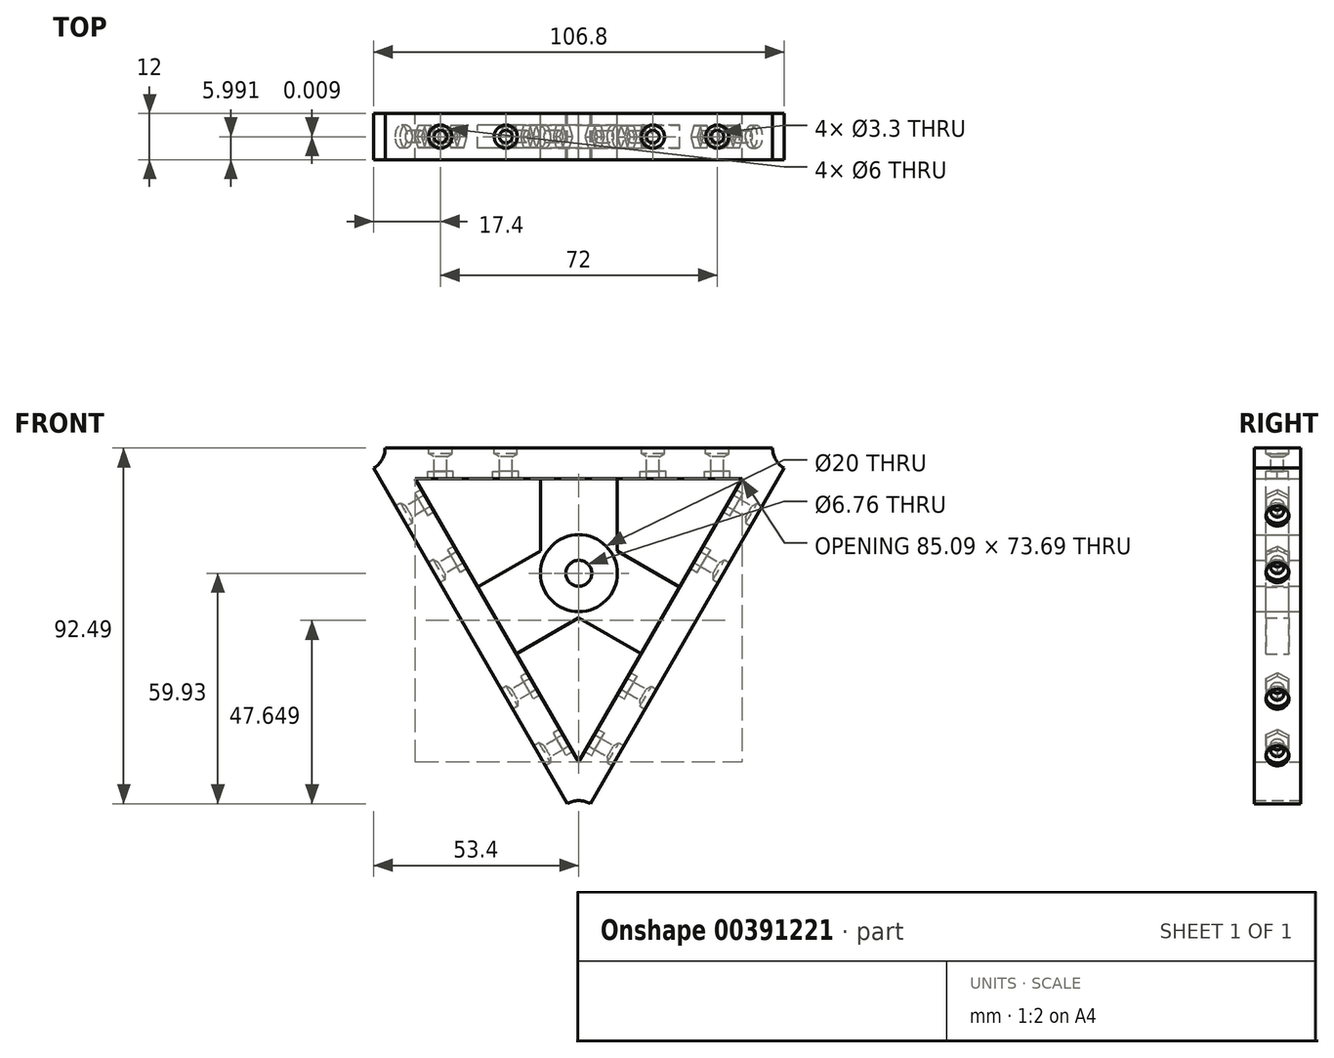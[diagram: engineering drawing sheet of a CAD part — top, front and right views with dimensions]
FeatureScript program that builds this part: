
annotation { "Feature Type Name" : "Feature", "Feature Type Description" : "" }
export const myFeature = defineFeature(function(context is Context, id is Id, definition is map)
    precondition{}
    {
        {
            var Q0;
            Q0=qCreatedBy(makeId("Front.planeOp"),FACE);
            var sketch = newSketch(context, id + "F0", { "sketchPlane" : qUnion([Q0])});
            skCircle(sketch, "E0.cCircle", {"center": v(0, 0) * mm, "radius": 32.56 * mm, "construction": true});
            skLineSegment(sketch, "E0.0", {"start": v(56.4, 32.56) * mm, "end": v(0, -65.13) * mm});
            skLineSegment(sketch, "E0.1", {"start": v(0, -65.13) * mm, "end": v(-56.4, 32.56) * mm});
            skLineSegment(sketch, "E0.2", {"start": v(-56.4, 32.56) * mm, "end": v(56.4, 32.56) * mm});
            skPoint(sketch, "E0.0.midPoint", {"position": v(28.2, -16.28) * mm});
            skCircle(sketch, "E1.cCircle", {"center": v(0, 0) * mm, "radius": 24.56 * mm, "construction": true});
            skLineSegment(sketch, "E1.0", {"start": v(42.54, 24.56) * mm, "end": v(0, -49.13) * mm});
            skLineSegment(sketch, "E1.1", {"start": v(0, -49.13) * mm, "end": v(-42.54, 24.56) * mm});
            skLineSegment(sketch, "E1.2", {"start": v(-42.54, 24.56) * mm, "end": v(42.54, 24.56) * mm});
            skPoint(sketch, "E1.0.midPoint", {"position": v(21.27, -12.28) * mm});
            skCircle(sketch, "E2", {"center": v(56.4, 32.56) * mm, "radius": 6 * mm});
            skCircle(sketch, "E3", {"center": v(-56.4, 32.56) * mm, "radius": 6 * mm});
            skCircle(sketch, "E4", {"center": v(0, -65.13) * mm, "radius": 6 * mm});
            skPoint(sketch, "E5", {"position": v(40.38, 48.53) * mm});
            skPoint(sketch, "E6", {"position": v(46.2, 14.9) * mm});
            skPoint(sketch, "E7", {"position": v(37.7, 0.17) * mm});
            skPoint(sketch, "E8", {"position": v(10.2, -47.46) * mm});
            skPoint(sketch, "E9", {"position": v(18.7, -32.74) * mm});
            skPoint(sketch, "E10", {"position": v(25.9, -20.26) * mm});
            skPoint(sketch, "E11", {"position": v(30.5, -12.3) * mm});
            skCircle(sketch, "E12", {"center": v(0, 0) * mm, "radius": 10 * mm});
            skLineSegment(sketch, "E13", {"start": v(-10, 0) * mm, "end": v(-10, 24.56) * mm});
            skLineSegment(sketch, "E14", {"start": v(10, 0) * mm, "end": v(10, 24.56) * mm});
            skLineSegment(sketch, "E15", {"start": v(5, 8.66) * mm, "end": v(26.27, -3.62) * mm});
            skLineSegment(sketch, "E16", {"start": v(-5, -8.66) * mm, "end": v(16.27, -20.94) * mm});
            skLineSegment(sketch, "E17", {"start": v(-5, 8.66) * mm, "end": v(-26.27, -3.62) * mm});
            skLineSegment(sketch, "E18", {"start": v(5, -8.66) * mm, "end": v(-16.27, -20.94) * mm});
            skSolve(sketch);
        }
        {
            var Q0;
            {var subQ9=sQuery(id+"F0.wireOp",EDGE,"E2");var subQ10=sQuery(id+"F0.wireOp",EDGE,"E0.0");var subQ11=makeQuery(id+"F0.imprint","INTERSECT",VERTEX,{"derivedFrom":[subQ10,subQ9]});Q0=makeQuery(id+"F0.imprint","IMPRINT",FACE,{"disambiguationData":[TD([[makeQuery(id+"F0.imprint","IMPRINT",EDGE,{"disambiguationData":[TD([[subQ11,-1.0]])],"derivedFrom":subQ10}),-1.0]])]});}
            var Q1;
            {var subQ0=sQuery(id+"F0.wireOp",EDGE,"E12");var subQ5=makeQuery(id+"F0.imprint","INTERSECT",VERTEX,{"derivedFrom":[subQ0,sQuery(id+"F0.wireOp",EDGE,"E14")]});Q1=makeQuery(id+"F0.imprint","IMPRINT",FACE,{"disambiguationData":[TD([[makeQuery(id+"F0.imprint","IMPRINT",EDGE,{"disambiguationData":[TD([[subQ5,-1.0]])],"derivedFrom":subQ0}),1.0]])]});}
            extrude(context, id + "F1", {"entities" : qUnion([Q0, Q1]), "depth" : 12 * mm});
        }
        {
            var Q0;
            {var subQ1=sQuery(id+"F0.wireOp",EDGE,"E1.2");var subQ9=sQuery(id+"F0.wireOp",EDGE,"E13");var subQ10=makeQuery(id+"F0.imprint","INTERSECT",VERTEX,{"derivedFrom":[subQ1,subQ9]});Q0=makeQuery(id+"F0.imprint","IMPRINT",FACE,{"disambiguationData":[TD([[makeQuery(id+"F0.imprint","IMPRINT",EDGE,{"disambiguationData":[TD([[subQ10,-1.0]])],"derivedFrom":subQ1}),-1.0]])]});}
            var Q1;
            {var subQ3=sQuery(id+"F0.wireOp",EDGE,"E15");var subQ5=sQuery(id+"F0.wireOp",EDGE,"E1.0");var subQ6=makeQuery(id+"F0.imprint","INTERSECT",VERTEX,{"derivedFrom":[subQ5,subQ3]});Q1=makeQuery(id+"F0.imprint","IMPRINT",FACE,{"disambiguationData":[TD([[makeQuery(id+"F0.imprint","IMPRINT",EDGE,{"disambiguationData":[TD([[subQ6,-1.0]])],"derivedFrom":subQ5}),-1.0]])]});}
            var Q2;
            {var subQ7=sQuery(id+"F0.wireOp",EDGE,"E17");var subQ9=sQuery(id+"F0.wireOp",EDGE,"E1.1");var subQ11=makeQuery(id+"F0.imprint","INTERSECT",VERTEX,{"derivedFrom":[subQ9,subQ7]});Q2=makeQuery(id+"F0.imprint","IMPRINT",FACE,{"disambiguationData":[TD([[makeQuery(id+"F0.imprint","IMPRINT",EDGE,{"disambiguationData":[TD([[subQ11,1.0]])],"derivedFrom":subQ9}),-1.0]])]});}
            var Q3;
            {var subQ0=sQuery(id+"F0.wireOp",EDGE,"E13");var subQ1=sQuery(id+"F0.wireOp",EDGE,"E12");var subQ2=makeQuery(id+"F0.imprint","INTERSECT",VERTEX,{"derivedFrom":[subQ1,subQ0]});Q3=makeQuery(id+"F0.imprint","IMPRINT",FACE,{"disambiguationData":[TD([[makeQuery(id+"F0.imprint","IMPRINT",EDGE,{"disambiguationData":[TD([[subQ2,1.0]])],"derivedFrom":subQ1}),-1.0]])]});}
            var Q4;
            {var subQ0=sQuery(id+"F0.wireOp",EDGE,"E14");var subQ1=sQuery(id+"F0.wireOp",EDGE,"E12");var subQ2=makeQuery(id+"F0.imprint","INTERSECT",VERTEX,{"derivedFrom":[subQ1,subQ0]});Q4=makeQuery(id+"F0.imprint","IMPRINT",FACE,{"disambiguationData":[TD([[makeQuery(id+"F0.imprint","IMPRINT",EDGE,{"disambiguationData":[TD([[subQ2,-1.0]])],"derivedFrom":subQ1}),-1.0]])]});}
            var Q5;
            {var subQ0=sQuery(id+"F0.wireOp",EDGE,"E16");var subQ1=sQuery(id+"F0.wireOp",EDGE,"E12");var subQ2=makeQuery(id+"F0.imprint","INTERSECT",VERTEX,{"derivedFrom":[subQ1,subQ0]});Q5=makeQuery(id+"F0.imprint","IMPRINT",FACE,{"disambiguationData":[TD([[makeQuery(id+"F0.imprint","IMPRINT",EDGE,{"disambiguationData":[TD([[subQ2,-1.0]])],"derivedFrom":subQ1}),-1.0]])]});}
            extrude(context, id + "F2", {"entities" : qUnion([Q0, Q1, Q2, Q3, Q4, Q5]), "depth" : 9 * mm, "hasSecondDirection" : true, "secondDirectionOppositeDirection" : false, "secondDirectionDepth" : 3 * mm});
        }
        {
            var Q0;
            Q0=sQuery(id+"F0.wireOp",VERTEX,"E12.center");
            var Q1;
            Q1=makeQuery(id+"F1.opExtrude","SWEPT_BODY",BODY,{"disambiguationData":[OSD([sQuery(id+"F0.wireOp",EDGE,"E12")])]});
            hole(context, id + "F3", {"style" : HoleStyle.SIMPLE, "endStyle" : HoleEndStyle.THROUGH, "oppositeDirection" : true, "standardTappedOrClearance" : lookupTablePath({ "standard" : "ANSI", "fit" : "Normal (ASME)", "size" : "1/4", "type" : "Clearance" }), "standardBlindInLast" : lookupTablePath({ "fit" : "Free", "standard" : "ANSI", "size" : "1/4", "type" : "Clearance" }), "holeDiameter" : 6.76 * mm, "tappedDepth" : 12 * mm, "tapClearance" : 3, "locations" : qUnion([Q0]), "scope" : qUnion([Q1])});
        }
        {
            var Q0;
            Q0=makeQuery(id+"F1.opExtrude","SWEPT_FACE",FACE,{"disambiguationData":[OSD([sQuery(id+"F0.wireOp",EDGE,"E0.1")])]});
            var sketch = newSketch(context, id + "F4", { "sketchPlane" : qUnion([Q0])});
            skPoint(sketch, "E19", {"position": v(6, 36) * mm});
            skPoint(sketch, "E19.positionSnap0", {"position": v(6, 50.4) * mm});
            skPoint(sketch, "E20", {"position": v(6, 19) * mm});
            skPoint(sketch, "E21", {"position": v(6, -36) * mm});
            skPoint(sketch, "E21.positionSnap0", {"position": v(6, -50.4) * mm});
            skPoint(sketch, "E22", {"position": v(6, -19) * mm});
            skCircle(sketch, "E23.cCircle", {"center": v(6, -36) * mm, "radius": 2.9 * mm, "construction": true});
            skLineSegment(sketch, "E23.0", {"start": v(6, -32.65) * mm, "end": v(8.9, -34.33) * mm});
            skLineSegment(sketch, "E23.1", {"start": v(8.9, -34.33) * mm, "end": v(8.9, -37.67) * mm});
            skLineSegment(sketch, "E23.2", {"start": v(8.9, -37.67) * mm, "end": v(6, -39.35) * mm});
            skLineSegment(sketch, "E23.3", {"start": v(6, -39.35) * mm, "end": v(3.1, -37.67) * mm});
            skLineSegment(sketch, "E23.4", {"start": v(3.1, -37.67) * mm, "end": v(3.1, -34.33) * mm});
            skLineSegment(sketch, "E23.5", {"start": v(3.1, -34.33) * mm, "end": v(6, -32.65) * mm});
            skPoint(sketch, "E23.0.midPoint", {"position": v(7.45, -33.49) * mm});
            skCircle(sketch, "E24.cCircle", {"center": v(6, -19) * mm, "radius": 2.9 * mm, "construction": true});
            skLineSegment(sketch, "E24.0", {"start": v(6, -22.35) * mm, "end": v(3.1, -20.67) * mm});
            skLineSegment(sketch, "E24.1", {"start": v(3.1, -20.67) * mm, "end": v(3.1, -17.33) * mm});
            skLineSegment(sketch, "E24.2", {"start": v(3.1, -17.33) * mm, "end": v(6, -15.65) * mm});
            skLineSegment(sketch, "E24.3", {"start": v(6, -15.65) * mm, "end": v(8.9, -17.33) * mm});
            skLineSegment(sketch, "E24.4", {"start": v(8.9, -17.33) * mm, "end": v(8.9, -20.67) * mm});
            skLineSegment(sketch, "E24.5", {"start": v(8.9, -20.67) * mm, "end": v(6, -22.35) * mm});
            skPoint(sketch, "E24.0.midPoint", {"position": v(4.55, -21.51) * mm});
            skCircle(sketch, "E25.cCircle", {"center": v(6, 19) * mm, "radius": 2.9 * mm, "construction": true});
            skLineSegment(sketch, "E25.0", {"start": v(8.9, 20.67) * mm, "end": v(8.9, 17.33) * mm});
            skLineSegment(sketch, "E25.1", {"start": v(8.9, 17.33) * mm, "end": v(6, 15.65) * mm});
            skLineSegment(sketch, "E25.2", {"start": v(6, 15.65) * mm, "end": v(3.1, 17.33) * mm});
            skLineSegment(sketch, "E25.3", {"start": v(3.1, 17.33) * mm, "end": v(3.1, 20.67) * mm});
            skLineSegment(sketch, "E25.4", {"start": v(3.1, 20.67) * mm, "end": v(6, 22.35) * mm});
            skLineSegment(sketch, "E25.5", {"start": v(6, 22.35) * mm, "end": v(8.9, 20.67) * mm});
            skPoint(sketch, "E25.0.midPoint", {"position": v(8.9, 19) * mm});
            skCircle(sketch, "E26.cCircle", {"center": v(6, 36) * mm, "radius": 2.9 * mm, "construction": true});
            skLineSegment(sketch, "E26.0", {"start": v(8.9, 34.33) * mm, "end": v(6, 32.65) * mm});
            skLineSegment(sketch, "E26.1", {"start": v(6, 32.65) * mm, "end": v(3.1, 34.33) * mm});
            skLineSegment(sketch, "E26.2", {"start": v(3.1, 34.33) * mm, "end": v(3.1, 37.67) * mm});
            skLineSegment(sketch, "E26.3", {"start": v(3.1, 37.67) * mm, "end": v(6, 39.35) * mm});
            skLineSegment(sketch, "E26.4", {"start": v(6, 39.35) * mm, "end": v(8.9, 37.67) * mm});
            skLineSegment(sketch, "E26.5", {"start": v(8.9, 37.67) * mm, "end": v(8.9, 34.33) * mm});
            skPoint(sketch, "E26.0.midPoint", {"position": v(7.45, 33.49) * mm});
            skSolve(sketch);
        }
        {
            var Q0;
            Q0 = qSketchRegion(id + "F4", true);
            extrude(context, id + "F5", {"entities" : qUnion([Q0]), "operationType" : NewBodyOperationType.REMOVE, "oppositeDirection" : true, "depth" : 10 * mm, "hasSecondDirection" : true, "secondDirectionOppositeDirection" : true, "secondDirectionDepth" : 6 * mm});
        }
        {
            var Q0;
            Q0=sQuery(id+"F4.wireOp",VERTEX,"E21");
            var Q1;
            Q1=sQuery(id+"F4.wireOp",VERTEX,"E22");
            var Q2;
            Q2=sQuery(id+"F4.wireOp",VERTEX,"E20");
            var Q3;
            Q3=sQuery(id+"F4.wireOp",VERTEX,"E26.cCircle.center");
            var Q4;
            Q4=makeQuery(id+"F1.opExtrude","SWEPT_BODY",BODY,{"disambiguationData":[OSD([sQuery(id+"F0.wireOp",EDGE,"E0.0"),sQuery(id+"F0.wireOp",EDGE,"E0.1"),sQuery(id+"F0.wireOp",EDGE,"E0.2"),sQuery(id+"F0.wireOp",EDGE,"E1.0"),sQuery(id+"F0.wireOp",EDGE,"E1.1"),sQuery(id+"F0.wireOp",EDGE,"E1.2"),sQuery(id+"F0.wireOp",EDGE,"E2"),sQuery(id+"F0.wireOp",EDGE,"E3"),sQuery(id+"F0.wireOp",EDGE,"E4")])]});
            var Q5;
            Q5=makeQuery(id+"F2.opExtrude","SWEPT_BODY",BODY,{"disambiguationData":[OSD([sQuery(id+"F0.wireOp",EDGE,"E1.0"),sQuery(id+"F0.wireOp",EDGE,"E1.1"),sQuery(id+"F0.wireOp",EDGE,"E1.2"),sQuery(id+"F0.wireOp",EDGE,"E12"),sQuery(id+"F0.wireOp",EDGE,"E13"),sQuery(id+"F0.wireOp",EDGE,"E14"),sQuery(id+"F0.wireOp",EDGE,"E15"),sQuery(id+"F0.wireOp",EDGE,"E16"),sQuery(id+"F0.wireOp",EDGE,"E17"),sQuery(id+"F0.wireOp",EDGE,"E18")])]});
            hole(context, id + "F6", {"style" : HoleStyle.SIMPLE, "endStyle" : HoleEndStyle.BLIND, "standardTappedOrClearance" : lookupTablePath({ "standard" : "ISO", "fit" : "Normal", "size" : "M3", "type" : "Clearance" }), "standardBlindInLast" : lookupTablePath({ "fit" : "Standard", "standard" : "ISO", "size" : "M3", "type" : "Clearance" }), "holeDiameter" : 3.3 * mm, "holeDepth" : 8 * mm, "tappedDepth" : 12 * mm, "tapClearance" : 3, "locations" : qUnion([Q0, Q1, Q2, Q3]), "scope" : qUnion([Q4, Q5])});
        }
        {
            var Q0;
            Q0=sQuery(id+"F4.wireOp",VERTEX,"E21");
            var Q1;
            Q1=sQuery(id+"F4.wireOp",VERTEX,"E24.cCircle.center");
            var Q2;
            Q2=sQuery(id+"F4.wireOp",VERTEX,"E20");
            var Q3;
            Q3=sQuery(id+"F4.wireOp",VERTEX,"E19");
            var Q4;
            Q4=makeQuery(id+"F1.opExtrude","SWEPT_BODY",BODY,{"disambiguationData":[OSD([sQuery(id+"F0.wireOp",EDGE,"E0.0"),sQuery(id+"F0.wireOp",EDGE,"E0.1"),sQuery(id+"F0.wireOp",EDGE,"E0.2"),sQuery(id+"F0.wireOp",EDGE,"E1.0"),sQuery(id+"F0.wireOp",EDGE,"E1.1"),sQuery(id+"F0.wireOp",EDGE,"E1.2"),sQuery(id+"F0.wireOp",EDGE,"E2"),sQuery(id+"F0.wireOp",EDGE,"E3"),sQuery(id+"F0.wireOp",EDGE,"E4")])]});
            hole(context, id + "F7", {"style" : HoleStyle.SIMPLE, "endStyle" : HoleEndStyle.BLIND, "holeDiameter" : 6 * mm, "holeDepth" : 1.5 * mm, "tappedDepth" : 12 * mm, "tapClearance" : 3, "locations" : qUnion([Q0, Q1, Q2, Q3]), "scope" : qUnion([Q4])});
        }
        {
            var Q0;
            Q0=makeQuery(id+"F1.opExtrude","SWEPT_FACE",FACE,{"disambiguationData":[OSD([sQuery(id+"F0.wireOp",EDGE,"E0.2")])]});
            var sketch = newSketch(context, id + "F8", { "sketchPlane" : qUnion([Q0])});
            skPoint(sketch, "E27.positionSnap0", {"position": v(50.4, -6) * mm});
            skPoint(sketch, "E28", {"position": v(19.27, -6) * mm});
            skPoint(sketch, "E29", {"position": v(-19, -6) * mm});
            skPoint(sketch, "E29.positionSnap0", {"position": v(-50.4, -6) * mm});
            skPoint(sketch, "E30", {"position": v(-36, -6) * mm});
            skCircle(sketch, "E31.cCircle", {"center": v(-36, -6) * mm, "radius": 2.9 * mm, "construction": true});
            skLineSegment(sketch, "E31.0", {"start": v(-32.65, -6) * mm, "end": v(-34.33, -8.9) * mm});
            skLineSegment(sketch, "E31.1", {"start": v(-34.33, -8.9) * mm, "end": v(-37.67, -8.9) * mm});
            skLineSegment(sketch, "E31.2", {"start": v(-37.67, -8.9) * mm, "end": v(-39.35, -6) * mm});
            skLineSegment(sketch, "E31.3", {"start": v(-39.35, -6) * mm, "end": v(-37.67, -3.1) * mm});
            skLineSegment(sketch, "E31.4", {"start": v(-37.67, -3.1) * mm, "end": v(-34.33, -3.1) * mm});
            skLineSegment(sketch, "E31.5", {"start": v(-34.33, -3.1) * mm, "end": v(-32.65, -6) * mm});
            skPoint(sketch, "E31.0.midPoint", {"position": v(-33.49, -7.45) * mm});
            skCircle(sketch, "E32.cCircle", {"center": v(-19, -6) * mm, "radius": 2.9 * mm, "construction": true});
            skLineSegment(sketch, "E32.0", {"start": v(-17.33, -8.9) * mm, "end": v(-20.67, -8.9) * mm});
            skLineSegment(sketch, "E32.1", {"start": v(-20.67, -8.9) * mm, "end": v(-22.35, -6) * mm});
            skLineSegment(sketch, "E32.2", {"start": v(-22.35, -6) * mm, "end": v(-20.67, -3.1) * mm});
            skLineSegment(sketch, "E32.3", {"start": v(-20.67, -3.1) * mm, "end": v(-17.33, -3.1) * mm});
            skLineSegment(sketch, "E32.4", {"start": v(-17.33, -3.1) * mm, "end": v(-15.65, -6) * mm});
            skLineSegment(sketch, "E32.5", {"start": v(-15.65, -6) * mm, "end": v(-17.33, -8.9) * mm});
            skPoint(sketch, "E32.0.midPoint", {"position": v(-19, -8.9) * mm});
            skPoint(sketch, "E33", {"position": v(36, -6) * mm});
            skCircle(sketch, "E34.cCircle", {"center": v(36, -6) * mm, "radius": 2.9 * mm, "construction": true});
            skLineSegment(sketch, "E34.0", {"start": v(37.67, -8.9) * mm, "end": v(34.33, -8.9) * mm});
            skLineSegment(sketch, "E34.1", {"start": v(34.33, -8.9) * mm, "end": v(32.65, -6) * mm});
            skLineSegment(sketch, "E34.2", {"start": v(32.65, -6) * mm, "end": v(34.33, -3.1) * mm});
            skLineSegment(sketch, "E34.3", {"start": v(34.33, -3.1) * mm, "end": v(37.67, -3.1) * mm});
            skLineSegment(sketch, "E34.4", {"start": v(37.67, -3.1) * mm, "end": v(39.35, -6) * mm});
            skLineSegment(sketch, "E34.5", {"start": v(39.35, -6) * mm, "end": v(37.67, -8.9) * mm});
            skPoint(sketch, "E34.0.midPoint", {"position": v(36, -8.9) * mm});
            skCircle(sketch, "E35.cCircle", {"center": v(19.27, -6) * mm, "radius": 2.9 * mm, "construction": true});
            skLineSegment(sketch, "E35.0", {"start": v(22.62, -6) * mm, "end": v(20.94, -8.9) * mm});
            skLineSegment(sketch, "E35.1", {"start": v(20.94, -8.9) * mm, "end": v(17.6, -8.9) * mm});
            skLineSegment(sketch, "E35.2", {"start": v(17.6, -8.9) * mm, "end": v(15.92, -6) * mm});
            skLineSegment(sketch, "E35.3", {"start": v(15.92, -6) * mm, "end": v(17.6, -3.1) * mm});
            skLineSegment(sketch, "E35.4", {"start": v(17.6, -3.1) * mm, "end": v(20.94, -3.1) * mm});
            skLineSegment(sketch, "E35.5", {"start": v(20.94, -3.1) * mm, "end": v(22.62, -6) * mm});
            skPoint(sketch, "E35.0.midPoint", {"position": v(21.78, -7.46) * mm});
            skSolve(sketch);
        }
        {
            var Q0;
            Q0 = qSketchRegion(id + "F8", true);
            extrude(context, id + "F9", {"entities" : qUnion([Q0]), "operationType" : NewBodyOperationType.REMOVE, "oppositeDirection" : true, "depth" : 10 * mm, "hasSecondDirection" : true, "secondDirectionOppositeDirection" : true, "secondDirectionDepth" : 6 * mm});
        }
        {
            var Q0;
            Q0=sQuery(id+"F8.wireOp",VERTEX,"E31.cCircle.center");
            var Q1;
            Q1=sQuery(id+"F8.wireOp",VERTEX,"E29");
            var Q2;
            Q2=sQuery(id+"F8.wireOp",VERTEX,"E28");
            var Q3;
            Q3=sQuery(id+"F8.wireOp",VERTEX,"E34.cCircle.center");
            var Q4;
            Q4=makeQuery(id+"F1.opExtrude","SWEPT_BODY",BODY,{"disambiguationData":[OSD([sQuery(id+"F0.wireOp",EDGE,"E0.0"),sQuery(id+"F0.wireOp",EDGE,"E0.1"),sQuery(id+"F0.wireOp",EDGE,"E0.2"),sQuery(id+"F0.wireOp",EDGE,"E1.0"),sQuery(id+"F0.wireOp",EDGE,"E1.1"),sQuery(id+"F0.wireOp",EDGE,"E1.2"),sQuery(id+"F0.wireOp",EDGE,"E2"),sQuery(id+"F0.wireOp",EDGE,"E3"),sQuery(id+"F0.wireOp",EDGE,"E4")])]});
            hole(context, id + "F10", {"style" : HoleStyle.SIMPLE, "endStyle" : HoleEndStyle.BLIND, "standardTappedOrClearance" : lookupTablePath({ "standard" : "ISO", "fit" : "Normal", "size" : "M3", "type" : "Clearance" }), "standardBlindInLast" : lookupTablePath({ "fit" : "Standard", "standard" : "ISO", "size" : "M3", "type" : "Clearance" }), "holeDiameter" : 3.3 * mm, "holeDepth" : 8 * mm, "tappedDepth" : 12 * mm, "tapClearance" : 3, "locations" : qUnion([Q0, Q1, Q2, Q3]), "scope" : qUnion([Q4])});
        }
        {
            var Q0;
            Q0=sQuery(id+"F8.wireOp",VERTEX,"E30");
            var Q1;
            Q1=sQuery(id+"F8.wireOp",VERTEX,"E32.cCircle.center");
            var Q2;
            Q2=sQuery(id+"F8.wireOp",VERTEX,"E28");
            var Q3;
            Q3=sQuery(id+"F8.wireOp",VERTEX,"E33");
            var Q4;
            Q4=makeQuery(id+"F1.opExtrude","SWEPT_BODY",BODY,{"disambiguationData":[OSD([sQuery(id+"F0.wireOp",EDGE,"E0.0"),sQuery(id+"F0.wireOp",EDGE,"E0.1"),sQuery(id+"F0.wireOp",EDGE,"E0.2"),sQuery(id+"F0.wireOp",EDGE,"E1.0"),sQuery(id+"F0.wireOp",EDGE,"E1.1"),sQuery(id+"F0.wireOp",EDGE,"E1.2"),sQuery(id+"F0.wireOp",EDGE,"E2"),sQuery(id+"F0.wireOp",EDGE,"E3"),sQuery(id+"F0.wireOp",EDGE,"E4")])]});
            hole(context, id + "F11", {"style" : HoleStyle.SIMPLE, "endStyle" : HoleEndStyle.BLIND, "holeDiameter" : 6 * mm, "holeDepth" : 1.5 * mm, "tappedDepth" : 12 * mm, "tapClearance" : 3, "locations" : qUnion([Q0, Q1, Q2, Q3]), "scope" : qUnion([Q4])});
        }
        {
            var Q0;
            Q0=makeQuery(id+"F1.opExtrude","SWEPT_FACE",FACE,{"disambiguationData":[OSD([sQuery(id+"F0.wireOp",EDGE,"E0.0")])]});
            var sketch = newSketch(context, id + "F12", { "sketchPlane" : qUnion([Q0])});
            skPoint(sketch, "E36", {"position": v(-6, -36) * mm});
            skPoint(sketch, "E36.positionSnap0", {"position": v(-6, -50.4) * mm});
            skPoint(sketch, "E37", {"position": v(-6, -19) * mm});
            skPoint(sketch, "E38", {"position": v(-6, 36) * mm});
            skPoint(sketch, "E38.positionSnap0", {"position": v(-6, 50.4) * mm});
            skPoint(sketch, "E39", {"position": v(-6, 19) * mm});
            skCircle(sketch, "E40.cCircle", {"center": v(-6, 36) * mm, "radius": 2.9 * mm, "construction": true});
            skLineSegment(sketch, "E40.0", {"start": v(-6, 32.65) * mm, "end": v(-8.9, 34.33) * mm});
            skLineSegment(sketch, "E40.1", {"start": v(-8.9, 34.33) * mm, "end": v(-8.9, 37.67) * mm});
            skLineSegment(sketch, "E40.2", {"start": v(-8.9, 37.67) * mm, "end": v(-6, 39.35) * mm});
            skLineSegment(sketch, "E40.3", {"start": v(-6, 39.35) * mm, "end": v(-3.1, 37.67) * mm});
            skLineSegment(sketch, "E40.4", {"start": v(-3.1, 37.67) * mm, "end": v(-3.1, 34.33) * mm});
            skLineSegment(sketch, "E40.5", {"start": v(-3.1, 34.33) * mm, "end": v(-6, 32.65) * mm});
            skPoint(sketch, "E40.0.midPoint", {"position": v(-7.45, 33.49) * mm});
            skCircle(sketch, "E41.cCircle", {"center": v(-6, 19) * mm, "radius": 2.9 * mm, "construction": true});
            skLineSegment(sketch, "E41.0", {"start": v(-6, 22.35) * mm, "end": v(-3.1, 20.67) * mm});
            skLineSegment(sketch, "E41.1", {"start": v(-3.1, 20.67) * mm, "end": v(-3.1, 17.33) * mm});
            skLineSegment(sketch, "E41.2", {"start": v(-3.1, 17.33) * mm, "end": v(-6, 15.65) * mm});
            skLineSegment(sketch, "E41.3", {"start": v(-6, 15.65) * mm, "end": v(-8.9, 17.33) * mm});
            skLineSegment(sketch, "E41.4", {"start": v(-8.9, 17.33) * mm, "end": v(-8.9, 20.67) * mm});
            skLineSegment(sketch, "E41.5", {"start": v(-8.9, 20.67) * mm, "end": v(-6, 22.35) * mm});
            skPoint(sketch, "E41.0.midPoint", {"position": v(-4.55, 21.51) * mm});
            skCircle(sketch, "E42.cCircle", {"center": v(-6, -19) * mm, "radius": 2.9 * mm, "construction": true});
            skLineSegment(sketch, "E42.0", {"start": v(-8.9, -17.33) * mm, "end": v(-6, -15.65) * mm});
            skLineSegment(sketch, "E42.1", {"start": v(-6, -15.65) * mm, "end": v(-3.1, -17.33) * mm});
            skLineSegment(sketch, "E42.2", {"start": v(-3.1, -17.33) * mm, "end": v(-3.1, -20.67) * mm});
            skLineSegment(sketch, "E42.3", {"start": v(-3.1, -20.67) * mm, "end": v(-6, -22.35) * mm});
            skLineSegment(sketch, "E42.4", {"start": v(-6, -22.35) * mm, "end": v(-8.9, -20.67) * mm});
            skLineSegment(sketch, "E42.5", {"start": v(-8.9, -20.67) * mm, "end": v(-8.9, -17.33) * mm});
            skPoint(sketch, "E42.0.midPoint", {"position": v(-7.45, -16.49) * mm});
            skCircle(sketch, "E43.cCircle", {"center": v(-6, -36) * mm, "radius": 2.9 * mm, "construction": true});
            skLineSegment(sketch, "E43.0", {"start": v(-8.9, -34.33) * mm, "end": v(-6, -32.65) * mm});
            skLineSegment(sketch, "E43.1", {"start": v(-6, -32.65) * mm, "end": v(-3.1, -34.33) * mm});
            skLineSegment(sketch, "E43.2", {"start": v(-3.1, -34.33) * mm, "end": v(-3.1, -37.67) * mm});
            skLineSegment(sketch, "E43.3", {"start": v(-3.1, -37.67) * mm, "end": v(-6, -39.35) * mm});
            skLineSegment(sketch, "E43.4", {"start": v(-6, -39.35) * mm, "end": v(-8.9, -37.67) * mm});
            skLineSegment(sketch, "E43.5", {"start": v(-8.9, -37.67) * mm, "end": v(-8.9, -34.33) * mm});
            skPoint(sketch, "E43.0.midPoint", {"position": v(-7.45, -33.49) * mm});
            skSolve(sketch);
        }
        {
            var Q0;
            Q0 = qSketchRegion(id + "F12", true);
            extrude(context, id + "F13", {"entities" : qUnion([Q0]), "operationType" : NewBodyOperationType.REMOVE, "oppositeDirection" : true, "depth" : 10 * mm, "hasSecondDirection" : true, "secondDirectionOppositeDirection" : true, "secondDirectionDepth" : 6 * mm});
        }
        {
            var Q0;
            Q0=sQuery(id+"F12.wireOp",VERTEX,"E38");
            var Q1;
            Q1=sQuery(id+"F12.wireOp",VERTEX,"E39");
            var Q2;
            Q2=sQuery(id+"F12.wireOp",VERTEX,"E37");
            var Q3;
            Q3=sQuery(id+"F12.wireOp",VERTEX,"E43.cCircle.center");
            var Q4;
            Q4=makeQuery(id+"F1.opExtrude","SWEPT_BODY",BODY,{"disambiguationData":[OSD([sQuery(id+"F0.wireOp",EDGE,"E0.0"),sQuery(id+"F0.wireOp",EDGE,"E0.1"),sQuery(id+"F0.wireOp",EDGE,"E0.2"),sQuery(id+"F0.wireOp",EDGE,"E1.0"),sQuery(id+"F0.wireOp",EDGE,"E1.1"),sQuery(id+"F0.wireOp",EDGE,"E1.2"),sQuery(id+"F0.wireOp",EDGE,"E2"),sQuery(id+"F0.wireOp",EDGE,"E3"),sQuery(id+"F0.wireOp",EDGE,"E4")])]});
            hole(context, id + "F14", {"style" : HoleStyle.SIMPLE, "endStyle" : HoleEndStyle.BLIND, "holeDiameter" : 6 * mm, "holeDepth" : 1.5 * mm, "tappedDepth" : 12 * mm, "tapClearance" : 3, "locations" : qUnion([Q0, Q1, Q2, Q3]), "scope" : qUnion([Q4])});
        }
        {
            var Q0;
            Q0=sQuery(id+"F12.wireOp",VERTEX,"E38");
            var Q1;
            Q1=sQuery(id+"F12.wireOp",VERTEX,"E41.cCircle.center");
            var Q2;
            Q2=sQuery(id+"F12.wireOp",VERTEX,"E37");
            var Q3;
            Q3=sQuery(id+"F12.wireOp",VERTEX,"E36");
            var Q4;
            Q4=makeQuery(id+"F1.opExtrude","SWEPT_BODY",BODY,{"disambiguationData":[OSD([sQuery(id+"F0.wireOp",EDGE,"E0.0"),sQuery(id+"F0.wireOp",EDGE,"E0.1"),sQuery(id+"F0.wireOp",EDGE,"E0.2"),sQuery(id+"F0.wireOp",EDGE,"E1.0"),sQuery(id+"F0.wireOp",EDGE,"E1.1"),sQuery(id+"F0.wireOp",EDGE,"E1.2"),sQuery(id+"F0.wireOp",EDGE,"E2"),sQuery(id+"F0.wireOp",EDGE,"E3"),sQuery(id+"F0.wireOp",EDGE,"E4")])]});
            hole(context, id + "F15", {"style" : HoleStyle.SIMPLE, "endStyle" : HoleEndStyle.BLIND, "standardTappedOrClearance" : lookupTablePath({ "standard" : "ISO", "fit" : "Normal", "size" : "M3", "type" : "Clearance" }), "standardBlindInLast" : lookupTablePath({ "fit" : "Standard", "standard" : "ISO", "size" : "M3", "type" : "Clearance" }), "holeDiameter" : 3.3 * mm, "holeDepth" : 8 * mm, "tappedDepth" : 12 * mm, "tapClearance" : 3, "locations" : qUnion([Q0, Q1, Q2, Q3]), "scope" : qUnion([Q4])});
        }
    });
